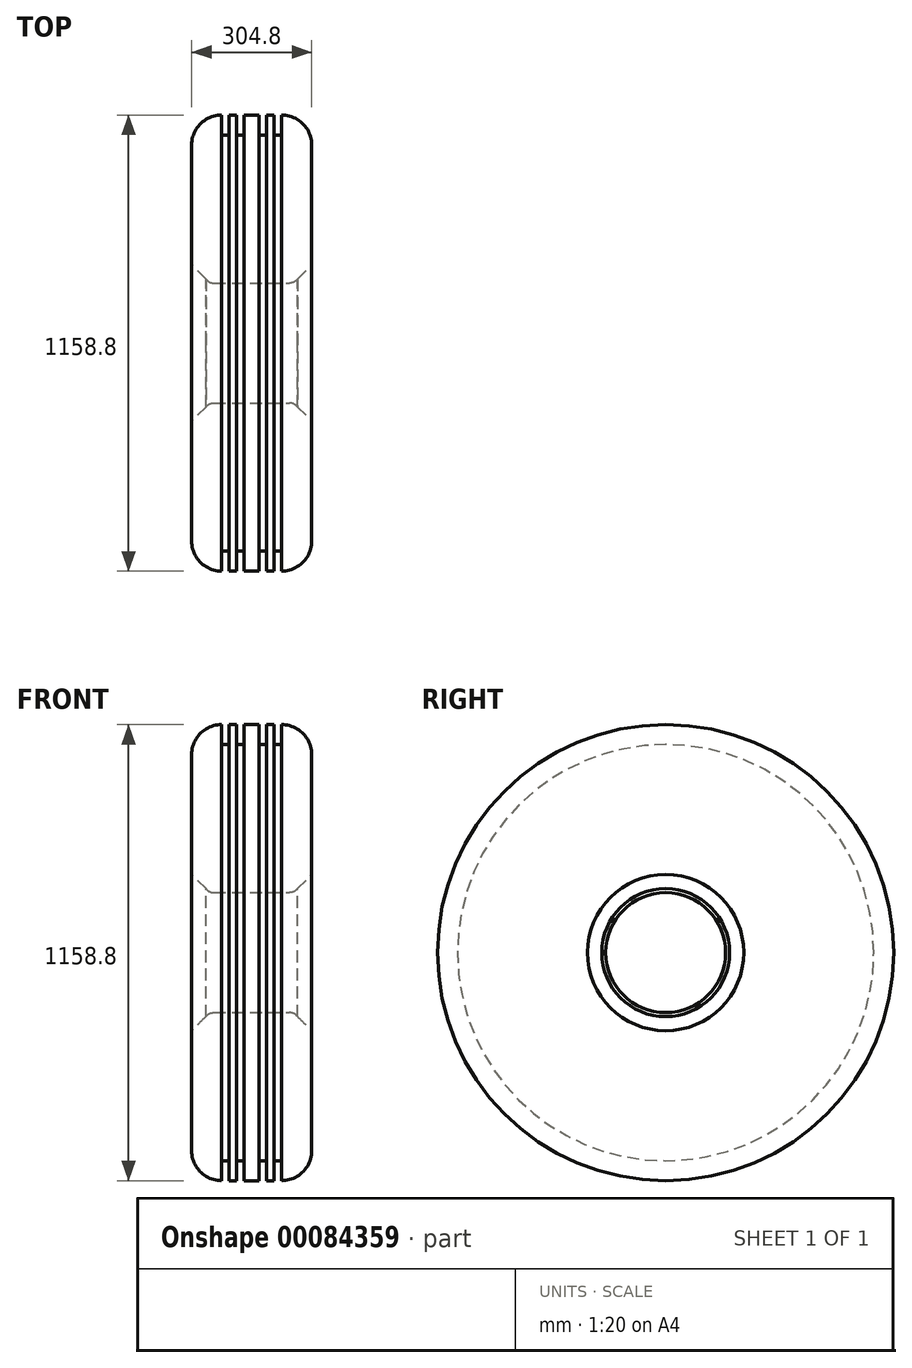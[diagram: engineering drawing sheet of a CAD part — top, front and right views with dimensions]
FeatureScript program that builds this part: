
annotation { "Feature Type Name" : "Feature", "Feature Type Description" : "" }
export const myFeature = defineFeature(function(context is Context, id is Id, definition is map)
    precondition{}
    {
        {
            var Q0;
            Q0=qCreatedBy(makeId("Front.planeOp"),FACE);
            var sketch = newSketch(context, id + "F0", { "sketchPlane" : qUnion([Q0])});
            skLineSegment(sketch, "E0", {"start": v(0, 0) * mm, "end": v(0, 427) * mm});
            skLineSegment(sketch, "E1", {"start": v(0, 427) * mm, "end": v(19.05, 427) * mm});
            skLineSegment(sketch, "E2", {"start": v(19.05, 427) * mm, "end": v(19.05, 376.2) * mm});
            skLineSegment(sketch, "E3", {"start": v(19.05, 376.2) * mm, "end": v(38.1, 376.2) * mm});
            skLineSegment(sketch, "E4", {"start": v(38.1, 376.2) * mm, "end": v(38.1, 427) * mm});
            skLineSegment(sketch, "E5", {"start": v(38.1, 427) * mm, "end": v(57.15, 427) * mm});
            skLineSegment(sketch, "E6", {"start": v(57.15, 427) * mm, "end": v(57.15, 376.2) * mm});
            skLineSegment(sketch, "E7", {"start": v(57.15, 376.2) * mm, "end": v(76.2, 376.2) * mm});
            skLineSegment(sketch, "E8", {"start": v(76.2, 376.2) * mm, "end": v(76.2, 427) * mm});
            skLineSegment(sketch, "E9", {"start": v(152.4, 350.8) * mm, "end": v(152.4, 46) * mm});
            skLineSegment(sketch, "E10", {"start": v(0, 0) * mm, "end": v(96.22, 0) * mm});
            skArc(sketch, "E11", {"start": v(116.48, 10.08) * mm, "mid": v(107.53, 2.66) * mm, "end": v(96.22, 0) * mm});
            skLineSegment(sketch, "E12", {"start": v(116.48, 10.08) * mm, "end": v(152.4, 46) * mm});
            skArc(sketch, "E13", {"start": v(76.2, 427) * mm, "mid": v(130.08, 404.68) * mm, "end": v(152.4, 350.8) * mm});
            skLineSegment(sketch, "E14", {"start": v(397.83, -152.4) * mm, "end": v(-182.43, -152.4) * mm, "construction": true});
            skSolve(sketch);
        }
        {
            var Q0;
            Q0=makeQuery(id+"F0.imprint","IMPRINT",FACE,{"disambiguationData":[TD([[makeQuery(id+"F0.imprint","IMPRINT",EDGE,{"derivedFrom":sQuery(id+"F0.wireOp",EDGE,"E0")}),-1.0]])]});
            var Q1;
            Q1=sQuery(id+"F0.wireOp",EDGE,"E14");
            revolve(context, id + "F1", {"entities" : qUnion([Q0]), "axis" : qUnion([Q1]), "revolveType" : RevolveType.FULL});
        }
        {
            var Q0;
            Q0=makeQuery(id+"F1.opRevolve","SWEPT_BODY",BODY,{"disambiguationData":[OSD([sQuery(id+"F0.wireOp",EDGE,"E0"),sQuery(id+"F0.wireOp",EDGE,"E1"),sQuery(id+"F0.wireOp",EDGE,"E2"),sQuery(id+"F0.wireOp",EDGE,"E3"),sQuery(id+"F0.wireOp",EDGE,"E4"),sQuery(id+"F0.wireOp",EDGE,"E5"),sQuery(id+"F0.wireOp",EDGE,"E6"),sQuery(id+"F0.wireOp",EDGE,"E7"),sQuery(id+"F0.wireOp",EDGE,"E8"),sQuery(id+"F0.wireOp",EDGE,"E9"),sQuery(id+"F0.wireOp",EDGE,"E10"),sQuery(id+"F0.wireOp",EDGE,"E11"),sQuery(id+"F0.wireOp",EDGE,"E12"),sQuery(id+"F0.wireOp",EDGE,"E13")])]});
            var Q1;
            Q1=makeQuery(id+"F1.opRevolve","SWEPT_FACE",FACE,{"disambiguationData":[OSD([sQuery(id+"F0.wireOp",EDGE,"E0")])]});
            mirror(context, id + "F2", {"operationType" : NewBodyOperationType.ADD, "entities" : qUnion([Q0]), "mirrorPlane" : qUnion([Q1])});
        }
    });
